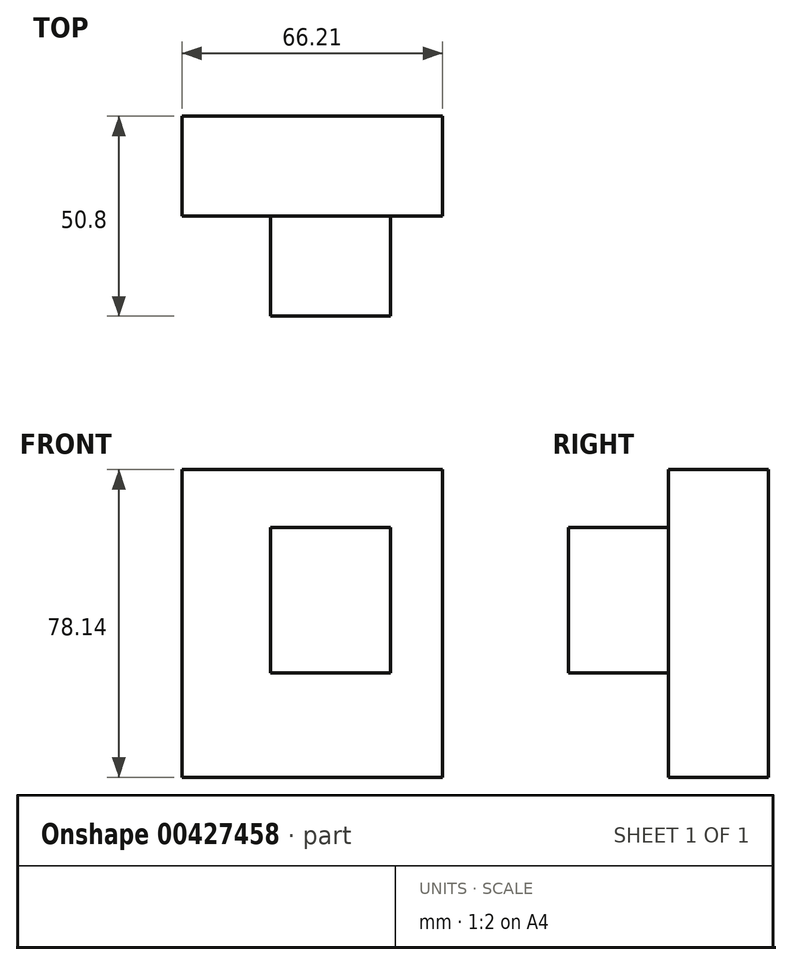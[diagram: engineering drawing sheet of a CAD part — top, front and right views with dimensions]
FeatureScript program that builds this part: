
annotation { "Feature Type Name" : "Feature", "Feature Type Description" : "" }
export const myFeature = defineFeature(function(context is Context, id is Id, definition is map)
    precondition{}
    {
        {
            var Q0;
            Q0=qCreatedBy(makeId("Front.planeOp"),FACE);
            var sketch = newSketch(context, id + "F0", { "sketchPlane" : qUnion([Q0])});
            skLineSegment(sketch, "E0.bottom", {"start": v(43.7, 31.92) * mm, "end": v(-22.51, 31.92) * mm});
            skLineSegment(sketch, "E0.top", {"start": v(43.7, -46.22) * mm, "end": v(-22.51, -46.22) * mm});
            skLineSegment(sketch, "E0.left", {"start": v(43.7, 31.92) * mm, "end": v(43.7, -46.22) * mm});
            skLineSegment(sketch, "E0.right", {"start": v(-22.51, 31.92) * mm, "end": v(-22.51, -46.22) * mm});
            skSolve(sketch);
        }
        {
            var Q0;
            Q0 = qSketchRegion(id + "F0", true);
            extrude(context, id + "F1", {"entities" : qUnion([Q0]), "depth" : 25.4 * mm});
        }
        {
            var Q0;
            Q0=makeQuery(id+"F1.opExtrude","CAP_FACE",FACE,{"disambiguationData":[OSD([sQuery(id+"F0.wireOp",EDGE,"E0.bottom"),sQuery(id+"F0.wireOp",EDGE,"E0.top"),sQuery(id+"F0.wireOp",EDGE,"E0.left"),sQuery(id+"F0.wireOp",EDGE,"E0.right")])],"isStart":false});
            var sketch = newSketch(context, id + "F2", { "sketchPlane" : qUnion([Q0])});
            skSolve(sketch);
        }
        {
            var Q0;
            Q0=makeQuery(id+"F2.imprint","IMPRINT",FACE,{"disambiguationData":[TD([[makeQuery(id+"F2.imprint","IMPRINT",EDGE,{"derivedFrom":makeQuery(id+"F1.opExtrude","CAP_EDGE",EDGE,{"disambiguationData":[OSD([sQuery(id+"F0.wireOp",EDGE,"E0.bottom")])],"isStart":false})}),1.0]])]});
            var sketch = newSketch(context, id + "F3", { "sketchPlane" : qUnion([Q0])});
            skSolve(sketch);
        }
        {
            var Q0;
            Q0=makeQuery(id+"F3.imprint","IMPRINT",FACE,{"disambiguationData":[TD([[makeQuery(id+"F3.imprint","IMPRINT",EDGE,{"derivedFrom":makeQuery(id+"F2.imprint","IMPRINT",EDGE,{"derivedFrom":makeQuery(id+"F1.opExtrude","CAP_EDGE",EDGE,{"disambiguationData":[OSD([sQuery(id+"F0.wireOp",EDGE,"E0.bottom")])],"isStart":false})})}),1.0]])]});
            var sketch = newSketch(context, id + "F4", { "sketchPlane" : qUnion([Q0])});
            skLineSegment(sketch, "E1.bottom", {"start": v(0, -19.68) * mm, "end": v(30.45, -19.68) * mm});
            skLineSegment(sketch, "E1.top", {"start": v(0, 17.22) * mm, "end": v(30.45, 17.22) * mm});
            skLineSegment(sketch, "E1.left", {"start": v(0, -19.68) * mm, "end": v(0, 17.22) * mm});
            skLineSegment(sketch, "E1.right", {"start": v(30.45, -19.68) * mm, "end": v(30.45, 17.22) * mm});
            skSolve(sketch);
        }
        {
            var Q0;
            Q0 = qSketchRegion(id + "F4", true);
            extrude(context, id + "F5", {"entities" : qUnion([Q0]), "operationType" : NewBodyOperationType.ADD, "depth" : 25.4 * mm});
        }
    });
